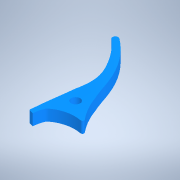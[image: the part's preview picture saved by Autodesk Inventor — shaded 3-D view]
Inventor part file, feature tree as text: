
AUTODESK INVENTOR PART (.ipt)
format: ipt  version: 2022 (Build 260153000, 153)  size: 148,992 bytes
history: native  units: mm
features: other x2, extrude x1, sketch x1
ambient origin geometry x8: Origin, YZ Plane, XZ Plane, XY Plane, X Axis, Y Axis, Z Axis, Center Point
bodies: Body1 (feature_tree)
feature tree (4):
  other  "Твердое тело1"
  other  "РабПлоскость1"
  extrude  "Выдавливание1"  Depth=5.0mm TaperAngle=0.0deg
  sketch  "Эскиз1"
